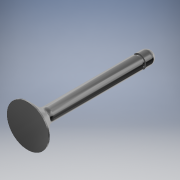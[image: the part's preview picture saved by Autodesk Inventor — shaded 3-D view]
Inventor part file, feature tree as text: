
AUTODESK INVENTOR PART (.ipt)
format: ipt  version: 2018 (Build 220112000, 112)  size: 130,560 bytes
history: native  units: mm
features: revolve x1, sketch x1
ambient origin geometry x8: Origin, YZ Plane, XZ Plane, XY Plane, X Axis, Y Axis, Z Axis, Center Point
bodies: Solid1 (feature_tree)
feature tree (2):
  revolve  "Revolution1"  [1 undecoded]
  sketch  "Sketch1"  dims[d1=4.75mm d2=1.5mm d3=0.3mm d4=45.0deg d5=1.5mm d6=1.15mm d8=0.65mm d9=1.4mm d10=27.0mm d11=2.5mm d12=90.0deg]
note: 1 required parameter value undecoded (feature->parameter linkage not recoverable at this tier; creation-order binding heuristic only, values carry confidence <= 0.55)
